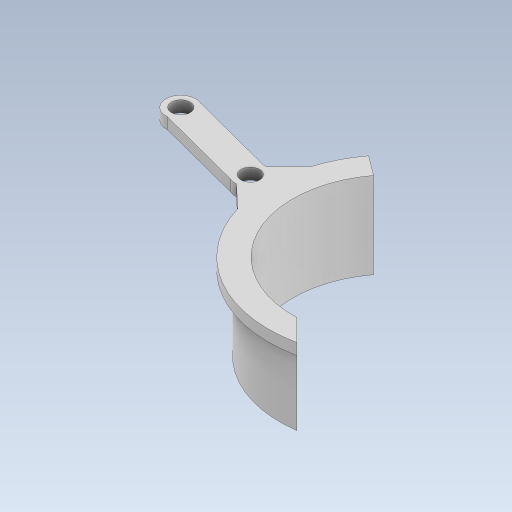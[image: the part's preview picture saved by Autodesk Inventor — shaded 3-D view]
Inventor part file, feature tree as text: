
AUTODESK INVENTOR PART (.ipt)
format: ipt  version: 2023.5 (Build 275446000, 446)  size: 301,056 bytes
history: native  units: mm
features: extrude x2, sketch x1
ambient origin geometry x8: Origin, YZ Plane, XZ Plane, XY Plane, X Axis, Y Axis, Z Axis, Center Point
bodies: Body1 (feature_tree)
feature tree (3):
  sketch  "Sketch1"  dims[d41=3.0mm d42=0.0mm d43=3.0mm d44=20.0mm d45=0.0mm d46=0.0mm d47=5.0mm d48=33.5mm d49=30.5mm d50=29.0mm d51=66.999922mm d52=5.883847mm d53=5.883847mm d54=25.572922mm d55=25.572922mm d56=8.0mm d57=5.0mm d58=8.0mm d59=54.0mm d60=20.0mm d61=45.0deg]
  extrude  "Extrusion5"  Depth=3.0mm TaperAngle=0.0deg
  extrude  "Extrusion6"  Depth=20.0mm
